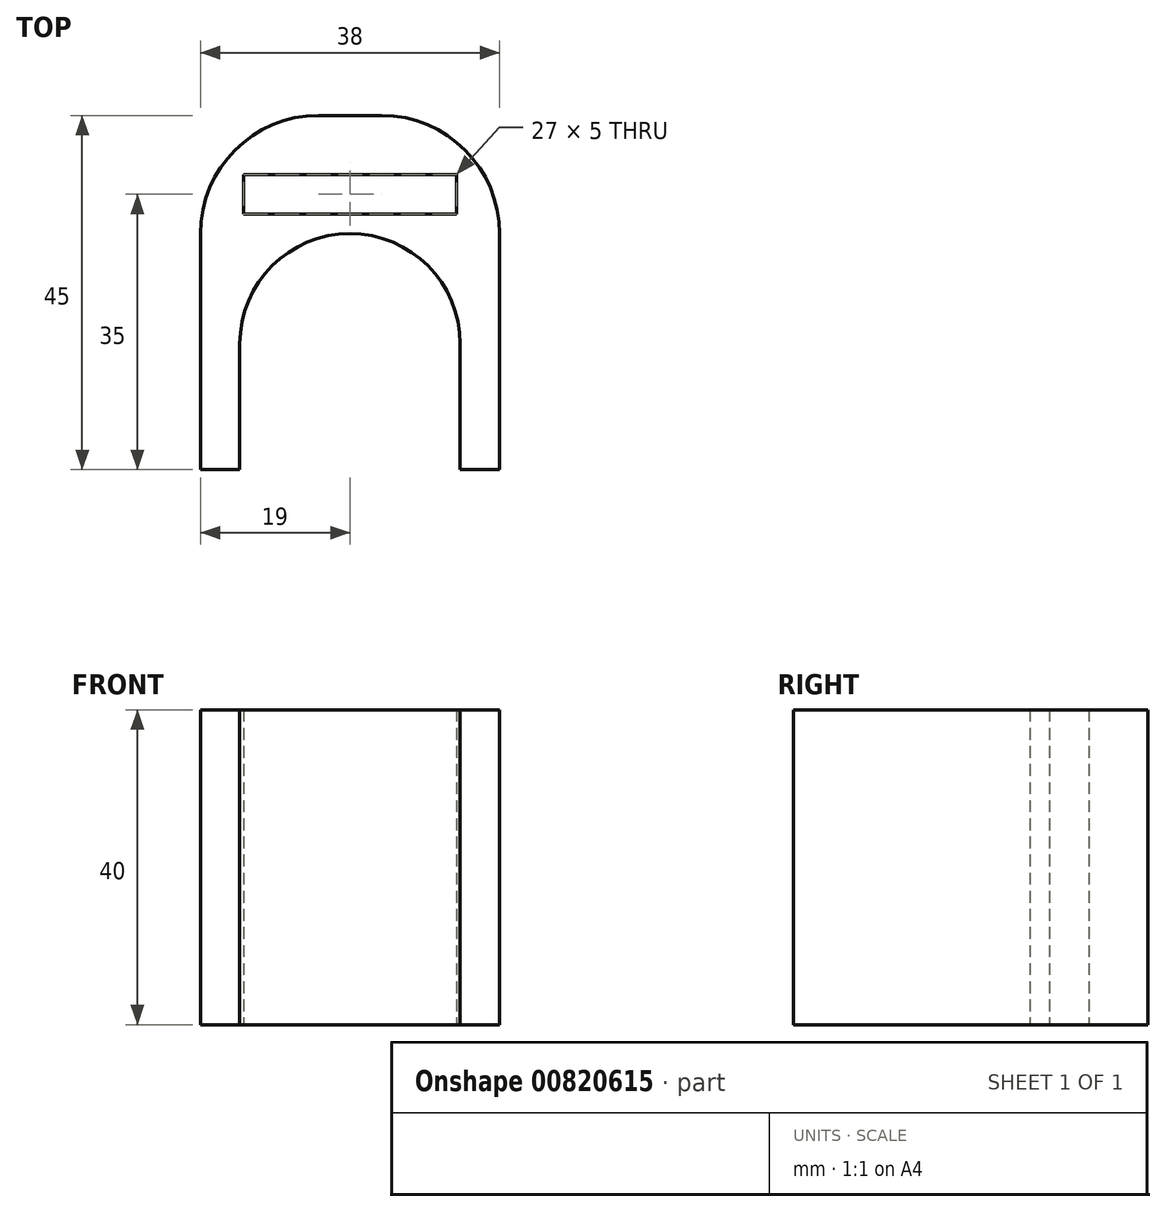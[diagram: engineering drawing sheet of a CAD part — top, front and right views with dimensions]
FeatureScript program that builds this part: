
annotation { "Feature Type Name" : "Feature", "Feature Type Description" : "" }
export const myFeature = defineFeature(function(context is Context, id is Id, definition is map)
    precondition{}
    {
        {
            var Q0;
            Q0=qCreatedBy(makeId("Top.planeOp"),FACE);
            var sketch = newSketch(context, id + "F0", { "sketchPlane" : qUnion([Q0])});
            skLineSegment(sketch, "E0", {"start": v(0, 0) * mm, "end": v(5, 0) * mm});
            skLineSegment(sketch, "E1", {"start": v(0, 0) * mm, "end": v(0, 30) * mm});
            skLineSegment(sketch, "E2", {"start": v(5, 0) * mm, "end": v(5, 16) * mm});
            skLineSegment(sketch, "E3", {"start": v(5, 0) * mm, "end": v(33, 0) * mm, "construction": true});
            skLineSegment(sketch, "E4", {"start": v(33, 0) * mm, "end": v(38, 0) * mm});
            skLineSegment(sketch, "E5", {"start": v(38, 0) * mm, "end": v(38, 30) * mm});
            skLineSegment(sketch, "E6", {"start": v(33, 0) * mm, "end": v(33, 16) * mm});
            skLineSegment(sketch, "E7", {"start": v(19, 30) * mm, "end": v(19, 30) * mm});
            skPoint(sketch, "E8.visualSharp", {"position": v(5, 30) * mm});
            skArc(sketch, "E8.filletArc", {"start": v(19, 30) * mm, "mid": v(9.1, 25.9) * mm, "end": v(5, 16) * mm});
            skPoint(sketch, "E9.visualSharp", {"position": v(33, 30) * mm});
            skArc(sketch, "E9.filletArc", {"start": v(33, 16) * mm, "mid": v(28.9, 25.9) * mm, "end": v(19, 30) * mm});
            skLineSegment(sketch, "E10", {"start": v(0, 30) * mm, "end": v(0, 30) * mm});
            skLineSegment(sketch, "E11", {"start": v(38, 30) * mm, "end": v(38, 30) * mm});
            skLineSegment(sketch, "E12", {"start": v(23, 45) * mm, "end": v(15, 45) * mm});
            skPoint(sketch, "E13.visualSharp", {"position": v(0, 45) * mm});
            skArc(sketch, "E13.filletArc", {"start": v(15, 45) * mm, "mid": v(4.4, 40.6) * mm, "end": v(0, 30) * mm});
            skPoint(sketch, "E14.visualSharp", {"position": v(38, 45) * mm});
            skArc(sketch, "E14.filletArc", {"start": v(38, 30) * mm, "mid": v(33.6, 40.6) * mm, "end": v(23, 45) * mm});
            skPoint(sketch, "E15.middle", {"position": v(18.5, 27.5) * mm});
            skLineSegment(sketch, "E16", {"start": v(19, 30) * mm, "end": v(19, 35) * mm, "construction": true});
            skLineSegment(sketch, "E17.bottom", {"start": v(32.5, 32.5) * mm, "end": v(5.5, 32.5) * mm});
            skLineSegment(sketch, "E17.top", {"start": v(32.5, 37.5) * mm, "end": v(5.5, 37.5) * mm});
            skLineSegment(sketch, "E17.left", {"start": v(32.5, 32.5) * mm, "end": v(32.5, 37.5) * mm});
            skLineSegment(sketch, "E17.right", {"start": v(5.5, 32.5) * mm, "end": v(5.5, 37.5) * mm});
            skPoint(sketch, "E17.middle", {"position": v(19, 35) * mm});
            skSolve(sketch);
        }
        {
            var Q0;
            Q0 = qSketchRegion(id + "F0", true);
            extrude(context, id + "F1", {"entities" : qUnion([Q0]), "depth" : 40 * mm, "offsetDistance" : 25 * mm});
        }
    });
